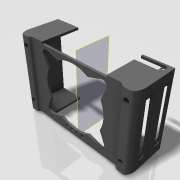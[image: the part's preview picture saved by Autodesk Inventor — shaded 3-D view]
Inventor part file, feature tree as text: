
AUTODESK INVENTOR PART (.ipt)
format: ipt  version: 2015 (Build 190159000, 159)  size: 822,272 bytes
history: native  units: in
note: dims shown in document units (in); Inventor stores cm internally (conversion verified against a paired STEP export)
features: extrude x21, sketch x16, fillet x13, reference x6, projected_geometry x4, mirror x3, plane x2
ambient origin geometry x8: Origin, YZ Plane, XZ Plane, XY Plane, X Axis, Y Axis, Z Axis, Center Point
bodies: Solid1 (feature_tree)
feature tree (65):
  extrude  "Extrusion1"  Depth=1.2598in TaperAngle=0.0deg
  extrude  "Extrusion3"  Depth=0.3937in
  extrude  "Extrusion2"  Depth=3.937in TaperAngle=0.0deg
  plane  "Work Plane1"
  extrude  "Extrusion23"  TaperAngle=0.0deg  [1 undecoded]
  extrude  "Extrusion4"  Depth=2.25in
  extrude  "Extrusion5"  Depth=0.15in
  extrude  "Extrusion6"  Depth=0.0984in TaperAngle=0.0deg
  sketch  "Sketch42"  dims[d59=2.2047in d62=0.0984in d63=0.0in]
  extrude  "Extrusion32"  Depth=0.1181in
  extrude  "Extrusion33"  Depth=0.0394in
  extrude  "Extrusion34"  Depth=0.6496in
  extrude  "Extrusion35"  Depth=0.2854in
  fillet  "Fillet12"  Radius=0.1969in
  fillet  "Fillet13"  [1 undecoded]
  extrude  "Extrusion39"  Depth=4.2362in
  extrude  "Extrusion40"  Depth=0.3937in TaperAngle=0.0deg
  fillet  "Fillet16"  Radius=0.3937in
  extrude  "Extrusion41"  Depth=0.2756in
  extrude  "Extrusion42"  Depth=0.2756in
  extrude  "Extrusion43"  Depth=0.0079in TaperAngle=0.0deg
  extrude  "Extrusion44"  TaperAngle=0.0deg  [1 undecoded]
  fillet  "Fillet19"  Radius=0.1575in
  fillet  "Fillet22"  Radius=0.1575in
  fillet  "Fillet23"  [1 undecoded]
  fillet  "Fillet24"  Radius=0.0787in
  extrude  "Extrusion45"  Depth=0.0079in TaperAngle=0.0deg
  extrude  "Extrusion46"  Depth=0.0079in
  plane  "Work Plane5"
  mirror  "Mirror2"
  extrude  "Extrusion47"  TaperAngle=0.0deg  [1 undecoded]
  fillet  "Fillet25"  Radius=0.0787in
  fillet  "Fillet26"  Radius=0.0079in
  extrude  "Extrusion48"  Depth=0.0079in
  fillet  "Fillet27"  Radius=0.1475in
  mirror  "Mirror3"
  fillet  "Fillet28"  Radius=0.88in
  fillet  "Fillet29"  Radius=1.7717in
  mirror  "Mirror4"
  fillet  "Fillet30"  Radius=0.1969in
  sketch  "Sketch2"  dims[d6=0.0787in d7=0.0in d9=1.2598in d10=0.0in]
  sketch  "Sketch4"  dims[d12=0.3937in d13=0.0in d28=2.2047in]
  reference  "Reference2"
  reference  "Reference3"
  reference  "Reference4"
  reference  "Reference5"
  sketch  "Sketch5"  dims[d29=2.2047in d31=3.937in d32=0.0in]
  reference  "Reference14"
  sketch  "Sketch6"  dims[d41=0.2756in d42=0.0in]
  sketch  "Sketch7"  dims[d44=0.1181in d47=2.25in]
  sketch  "Sketch28"  dims[d49=4.0in d50=0.15in]
  sketch  "Sketch43"  dims[d64=0.0787in d66=0.1181in]
  sketch  "Sketch46"  dims[d67=0.0394in d68=0.0394in]
  sketch  "Sketch52"  dims[d69=0.1575in d78=0.6496in]
  sketch  "Sketch54"  dims[d79=0.2854in d80=0.2854in d81=0.1969in d82=0.0in d191=-0.2756in]
  sketch  "Sketch55"  dims[d199=2.6772in d202=4.2362in]
  projected_geometry  "Projected Loop15"
  projected_geometry  "Projected Loop20"
  projected_geometry  "Projected Loop21"
  projected_geometry  "Projected Loop22"
  sketch  "Sketch56"  dims[d209=2.4409in d210=1.9685in d211=0.0in d308=0.3937in d309=0.0in]
  sketch  "Sketch57"  dims[d310=1.7717in d312=0.2756in]
  sketch  "Sketch59"  dims[d313=0.4488in d314=0.2756in]
  sketch  "Sketch60"  dims[d315=0.0787in d316=1.9685in d317=0.0in d330=0.0in d331=0.1575in d332=0.1575in d333=0.0in d334=0.0787in d335=0.0591in d336=0.0in d337=0.0787in d340=0.0in d341=0.0787in d342=0.0in d343=0.0079in d344=0.0079in d345=0.1102in d346=0.2756in d347=1.5748in d348=1.1002in d349=2.1in d350=1.95in d351=0.1102in d352=0.1102in d353=1.0651in d354=1.0651in d355=1.2179in d356=1.122in d357=1.0651in d358=0.1378in d359=1.0651in d360=1.122in d374=0.1475in d375=0.88in d400=1.7717in d401=0.2756in d402=0.0787in d404=0.4606in d405=0.1969in d406=0.0in d411=0.0787in d412=0.1575in d413=0.1575in d415=0.0in d416=0.0591in d417=0.0in d418=0.0079in d419=0.0787in d420=0.0787in d421=0.0787in d422=0.0in d423=0.2756in d425=0.0787in d426=0.7874in d429=0.3937in d430=0.0in d431=0.0787in d432=0.1575in d433=0.1575in d434=0.0591in d435=0.0in d436=0.0787in d437=0.0787in d438=0.0787in d439=0.0in d444=0.0079in d449=0.0118in d453=0.0118in d454=0.0787in d455=0.0787in d456=0.0787in d457=0.0787in d460=0.2953in d462=0.0787in d463=0.0787in d464=0.0787in d465=0.0787in d466=0.1969in d467=0.0709in d468=2.3756in d470=1.2598in d471=0.3937in d472=0.0in d473=2.3756in d475=1.5748in d476=0.0787in d477=0.0in d478=0.0709in d479=0.0787in d480=0.0787in d481=0.0787in d482=0.0787in d483=0.4567in d484=0.0787in d485=0.0787in d486=0.0787in d487=0.0787in d488=0.0787in d489=-2.1181in d490=0.1102in d491=0.1102in d492=0.1102in d493=0.1102in d494=0.315in d496=0.0984in d497=0.0in d498=0.1181in d499=0.4724in d500=0.1614in d501=0.1614in d502=0.1181in d503=0.0in d504=0.0079in d505=0.1181in d506=0.4724in d507=0.0079in]
  reference  "Reference16"
note: 5 required parameter values undecoded (feature->parameter linkage not recoverable at this tier; creation-order binding heuristic only, values carry confidence <= 0.55)
